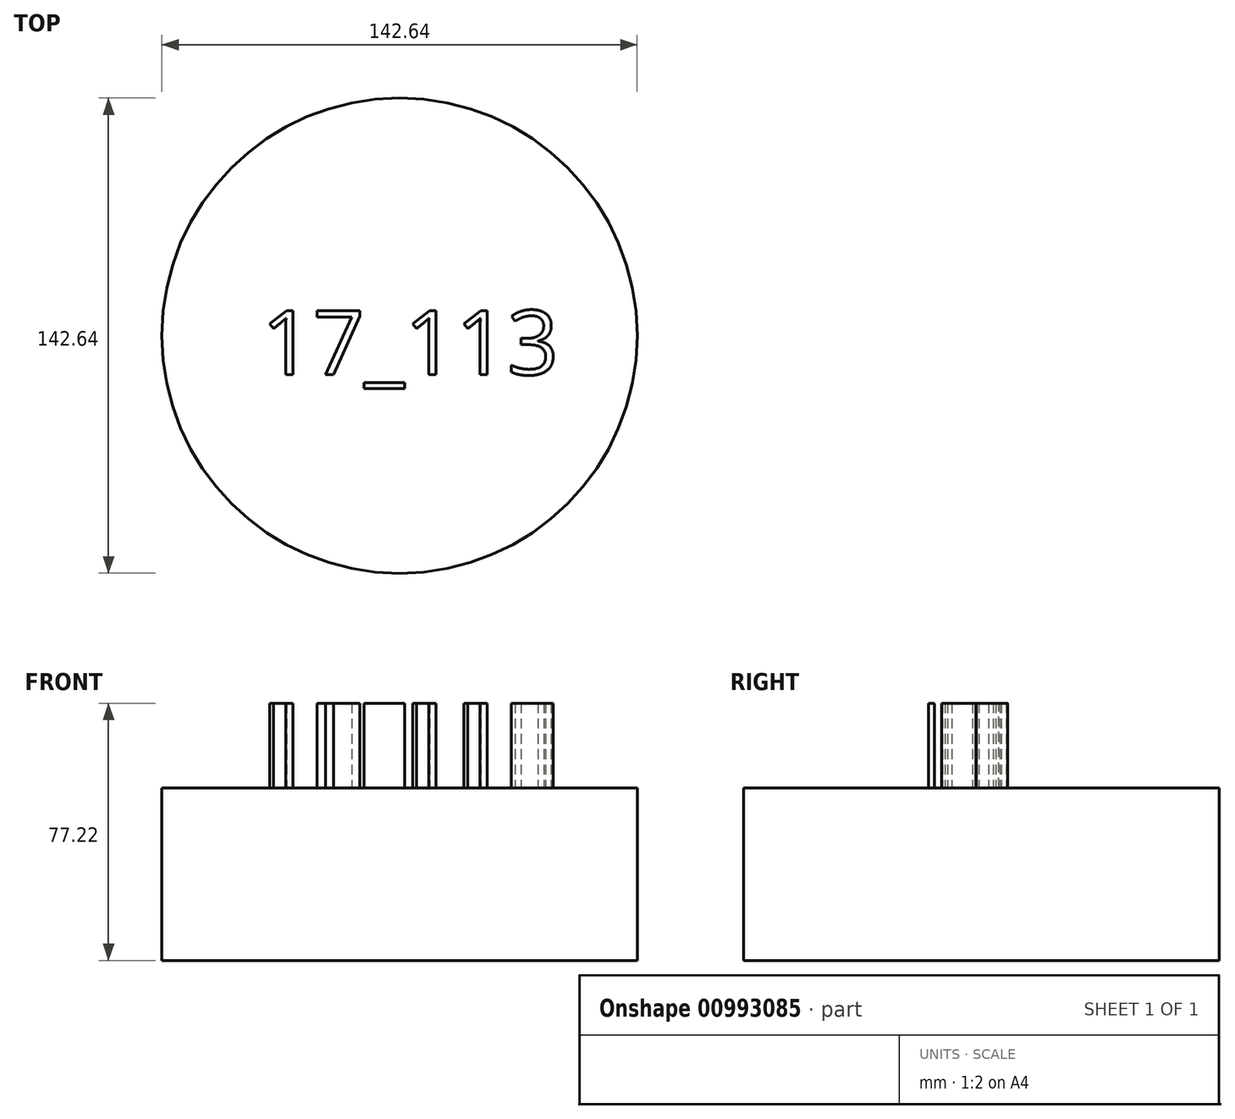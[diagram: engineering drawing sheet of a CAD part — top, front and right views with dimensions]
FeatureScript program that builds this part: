
annotation { "Feature Type Name" : "Feature", "Feature Type Description" : "" }
export const myFeature = defineFeature(function(context is Context, id is Id, definition is map)
    precondition{}
    {
        {
            var Q0;
            Q0=qCreatedBy(makeId("Top.planeOp"),FACE);
            var sketch = newSketch(context, id + "F0", { "sketchPlane" : qUnion([Q0])});
            skCircle(sketch, "E0", {"center": v(0, 0) * mm, "radius": 71.32 * mm});
            skSolve(sketch);
        }
        {
            var Q0;
            Q0=makeQuery(id+"F0.imprint","IMPRINT",FACE,{"disambiguationData":[TD([[makeQuery(id+"F0.imprint","IMPRINT",EDGE,{"derivedFrom":sQuery(id+"F0.wireOp",EDGE,"E0")}),1.0]])]});
            extrude(context, id + "F1", {"entities" : qUnion([Q0]), "depth" : 51.82 * mm, "offsetDistance" : 25.4 * mm});
        }
        {
            var Q0;
            Q0=makeQuery(id+"F1.opExtrude","CAP_FACE",FACE,{"disambiguationData":[OSD([sQuery(id+"F0.wireOp",EDGE,"E0")])],"isStart":false});
            var sketch = newSketch(context, id + "F2", { "sketchPlane" : qUnion([Q0])});
            skText(sketch, "E1", { "text": "17_113", "fontName": "OpenSans-Regular.ttf"});
            const initialGuessF2  = {"E1": [-0.04144, -0.0117, 1, 0, 0.01941]};
            skSetInitialGuess(sketch, initialGuessF2);
            skSolve(sketch);
        }
        {
            var Q0;
            Q0 = qSketchRegion(id + "F2", true);
            extrude(context, id + "F3", {"entities" : qUnion([Q0]), "operationType" : NewBodyOperationType.ADD, "depth" : 25.4 * mm, "offsetDistance" : 25.4 * mm});
        }
    });
